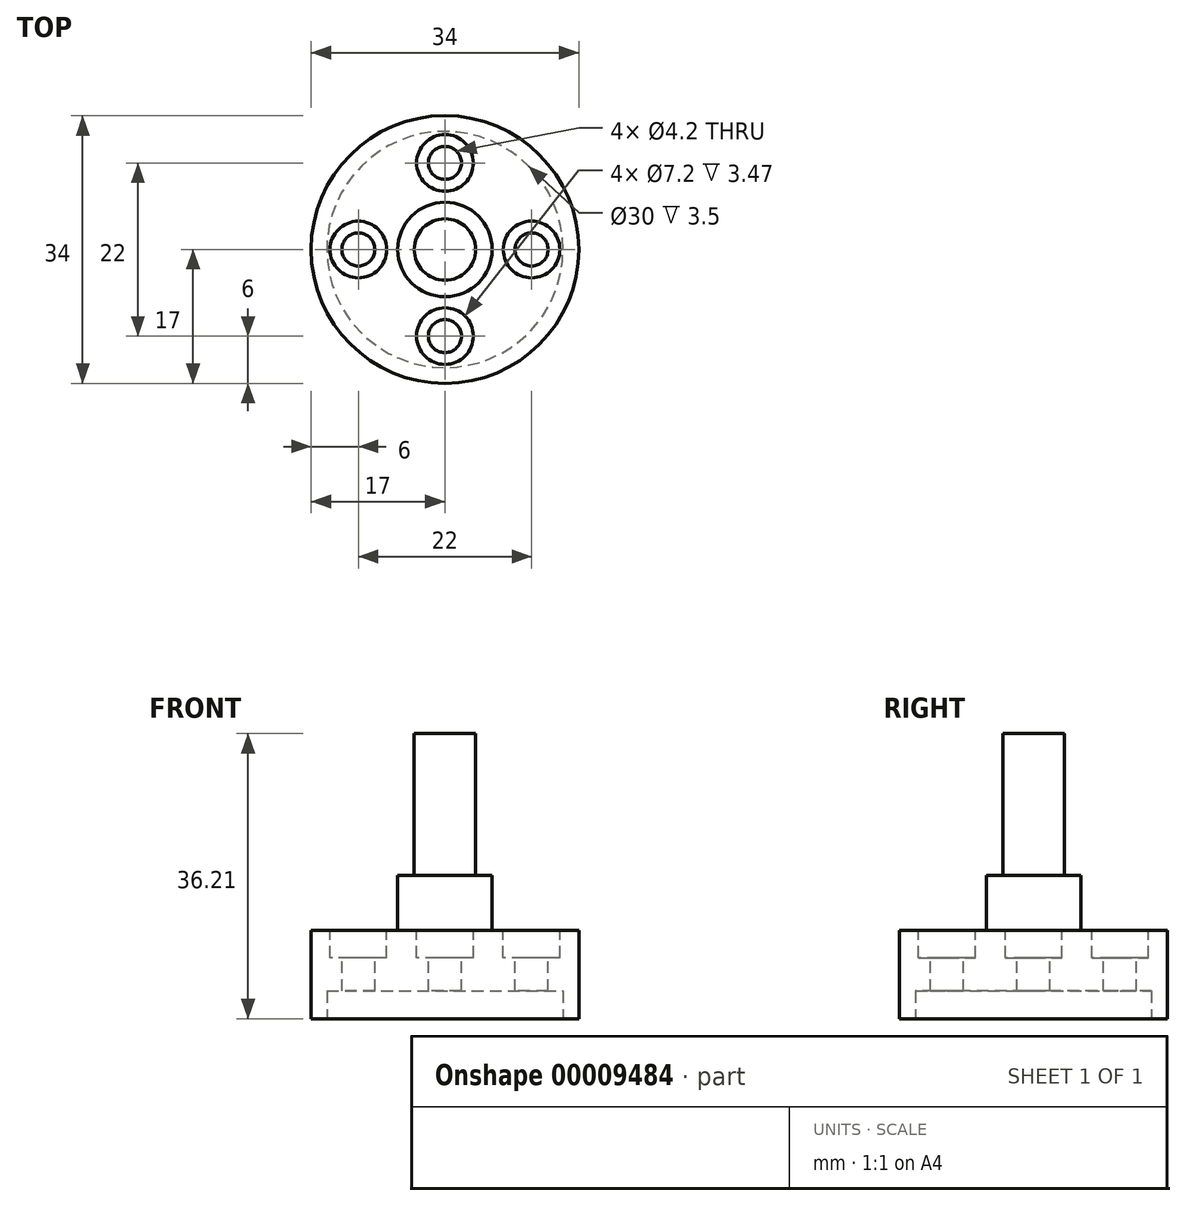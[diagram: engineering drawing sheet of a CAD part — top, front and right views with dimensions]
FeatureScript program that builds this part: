
annotation { "Feature Type Name" : "Feature", "Feature Type Description" : "" }
export const myFeature = defineFeature(function(context is Context, id is Id, definition is map)
    precondition{}
    {
        {
            var Q0;
            Q0=qCreatedBy(makeId("Front.planeOp"),FACE);
            var sketch = newSketch(context, id + "F0", { "sketchPlane" : qUnion([Q0])});
            skLineSegment(sketch, "E0", {"start": v(0, 0) * mm, "end": v(0, 32.7) * mm});
            skLineSegment(sketch, "E1", {"start": v(0, 32.7) * mm, "end": v(3.9, 32.7) * mm});
            skLineSegment(sketch, "E2", {"start": v(3.9, 32.7) * mm, "end": v(3.9, 14.7) * mm});
            skLineSegment(sketch, "E3", {"start": v(6, 7.7) * mm, "end": v(17, 7.71) * mm});
            skLineSegment(sketch, "E4", {"start": v(17, 7.71) * mm, "end": v(17, -3.5) * mm});
            skLineSegment(sketch, "E5", {"start": v(17, -3.5) * mm, "end": v(15, -3.5) * mm});
            skLineSegment(sketch, "E6", {"start": v(15, -3.5) * mm, "end": v(15, 0) * mm});
            skLineSegment(sketch, "E7", {"start": v(15, 0) * mm, "end": v(0, 0) * mm});
            skLineSegment(sketch, "E8", {"start": v(3.9, 14.7) * mm, "end": v(6, 14.7) * mm});
            skLineSegment(sketch, "E9", {"start": v(6, 14.7) * mm, "end": v(6, 7.7) * mm});
            skSolve(sketch);
        }
        {
            var Q0;
            Q0=makeQuery(id+"F0.imprint","IMPRINT",FACE,{"disambiguationData":[TD([[makeQuery(id+"F0.imprint","IMPRINT",EDGE,{"derivedFrom":sQuery(id+"F0.wireOp",EDGE,"E0")}),-1.0]])]});
            var Q1;
            Q1=sQuery(id+"F0.wireOp",EDGE,"E0");
            revolve(context, id + "F1", {"entities" : qUnion([Q0]), "axis" : qUnion([Q1]), "revolveType" : RevolveType.FULL});
        }
        {
            var Q0;
            Q0=makeQuery(id+"F1.opRevolve","SWEPT_FACE",FACE,{"disambiguationData":[OSD([sQuery(id+"F0.wireOp",EDGE,"E3")])]});
            var sketch = newSketch(context, id + "F2", { "sketchPlane" : qUnion([Q0])});
            skLineSegment(sketch, "E10", {"start": v(0, 0) * mm, "end": v(-11, 0) * mm});
            skLineSegment(sketch, "E11", {"start": v(0, 0) * mm, "end": v(0, -11) * mm});
            skLineSegment(sketch, "E12", {"start": v(0, 0) * mm, "end": v(11, 0) * mm});
            skLineSegment(sketch, "E13", {"start": v(0, 0) * mm, "end": v(0, 11) * mm});
            skSolve(sketch);
        }
        {
            var Q0;
            Q0=sQuery(id+"F2.wireOp",VERTEX,"E10.end");
            var Q1;
            Q1=sQuery(id+"F2.wireOp",VERTEX,"E13.end");
            var Q2;
            Q2=sQuery(id+"F2.wireOp",VERTEX,"E12.end");
            var Q3;
            Q3=sQuery(id+"F2.wireOp",VERTEX,"E11.end");
            var Q4;
            Q4=makeQuery(id+"F1.opRevolve","SWEPT_BODY",BODY,{"disambiguationData":[OSD([sQuery(id+"F0.wireOp",EDGE,"E0"),sQuery(id+"F0.wireOp",EDGE,"E1"),sQuery(id+"F0.wireOp",EDGE,"E2"),sQuery(id+"F0.wireOp",EDGE,"E3"),sQuery(id+"F0.wireOp",EDGE,"E4"),sQuery(id+"F0.wireOp",EDGE,"E5"),sQuery(id+"F0.wireOp",EDGE,"E6"),sQuery(id+"F0.wireOp",EDGE,"E7")])]});
            hole(context, id + "F3", {"style" : HoleStyle.C_BORE, "holeDiameter" : 4.2 * mm, "cBoreDiameter" : 7.2 * mm, "cBoreDepth" : 3.47 * mm, "endStyle" : HoleEndStyle.THROUGH, "locations" : qUnion([Q0, Q1, Q2, Q3]), "scope" : qUnion([Q4])});
        }
    });
